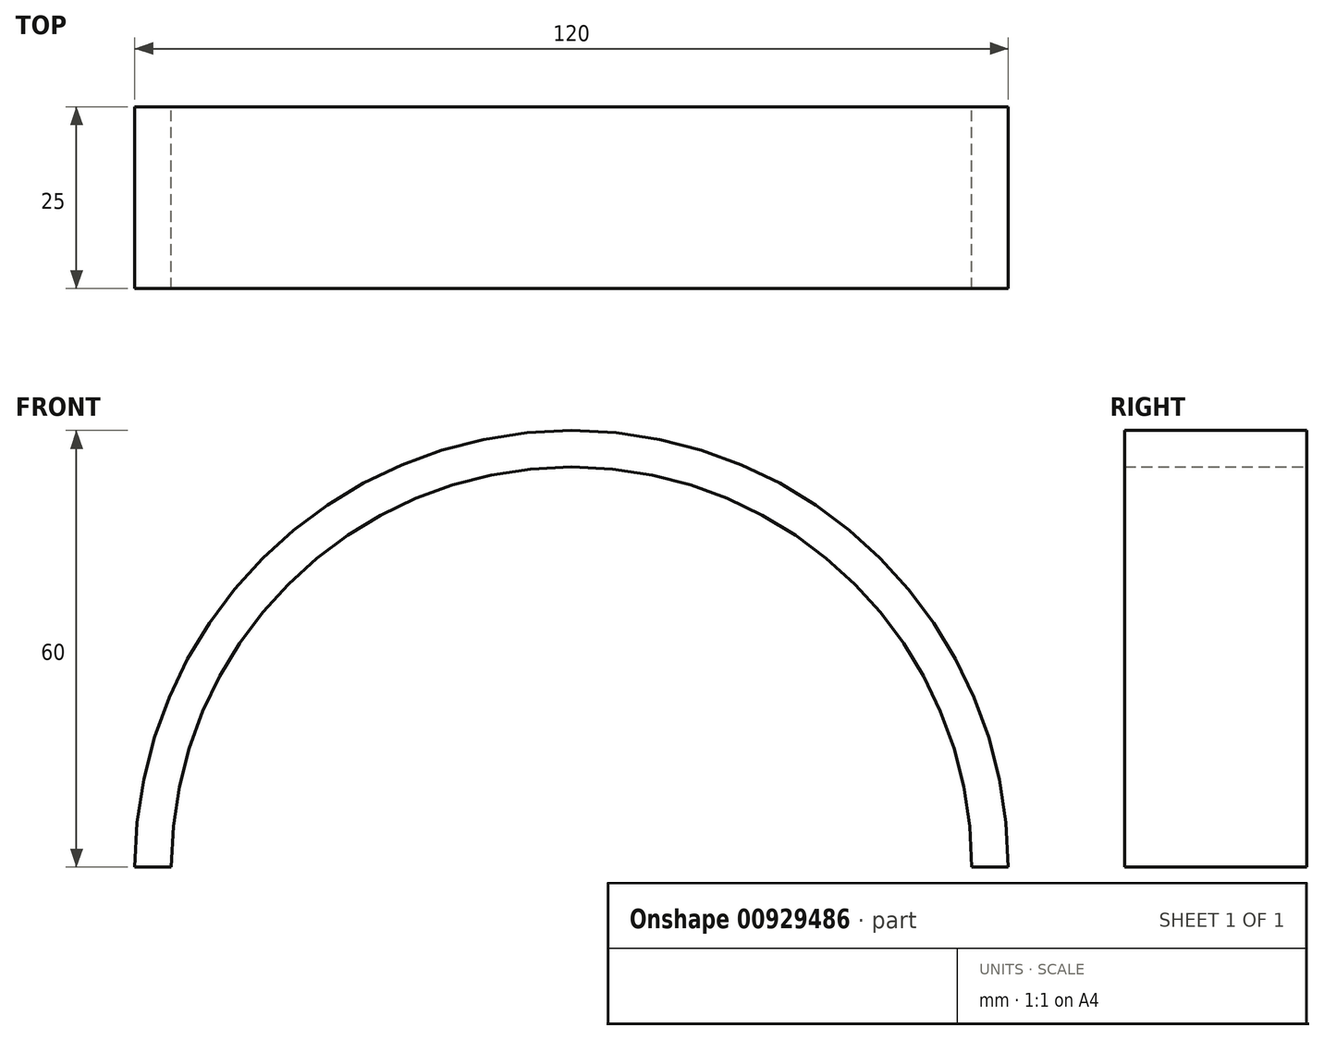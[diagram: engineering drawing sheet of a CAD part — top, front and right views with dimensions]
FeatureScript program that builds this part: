
annotation { "Feature Type Name" : "Feature", "Feature Type Description" : "" }
export const myFeature = defineFeature(function(context is Context, id is Id, definition is map)
    precondition{}
    {
        {
            var Q0;
            Q0=qCreatedBy(makeId("Front.planeOp"),FACE);
            var sketch = newSketch(context, id + "F0", { "sketchPlane" : qUnion([Q0])});
            skLineSegment(sketch, "E0", {"start": v(0, 0) * mm, "end": v(-60, 0) * mm, "construction": true});
            skLineSegment(sketch, "E1", {"start": v(0, 0) * mm, "end": v(60, 0) * mm, "construction": true});
            skArc(sketch, "E2", {"start": v(60, 0) * mm, "mid": v(0, 60) * mm, "end": v(-60, 0) * mm});
            skLineSegment(sketch, "E3", {"start": v(55, 0) * mm, "end": v(60, 0) * mm});
            skLineSegment(sketch, "E4", {"start": v(-60, 0) * mm, "end": v(-55, 0) * mm});
            skArc(sketch, "E5", {"start": v(55, 0) * mm, "mid": v(0, 55) * mm, "end": v(-55, 0) * mm});
            skSolve(sketch);
        }
        {
            var Q0;
            Q0=makeQuery(id+"F0.imprint","IMPRINT",FACE,{"disambiguationData":[TD([[makeQuery(id+"F0.imprint","IMPRINT",EDGE,{"derivedFrom":sQuery(id+"F0.wireOp",EDGE,"E2")}),1.0]])]});
            var Q1;
            Q1=makeQuery(id+"F0.imprint","IMPRINT",FACE,{"disambiguationData":[TD([[makeQuery(id+"F0.imprint","IMPRINT",EDGE,{"derivedFrom":sQuery(id+"F0.wireOp",EDGE,"ZrLSl4Js-G2I5-2LuC-DHkr-MJ2rNJ2JxYND")}),1.0]])]});
            extrude(context, id + "F1", {"entities" : qUnion([Q0, Q1]), "depth" : 25 * mm, "offsetDistance" : 25 * mm});
        }
    });
